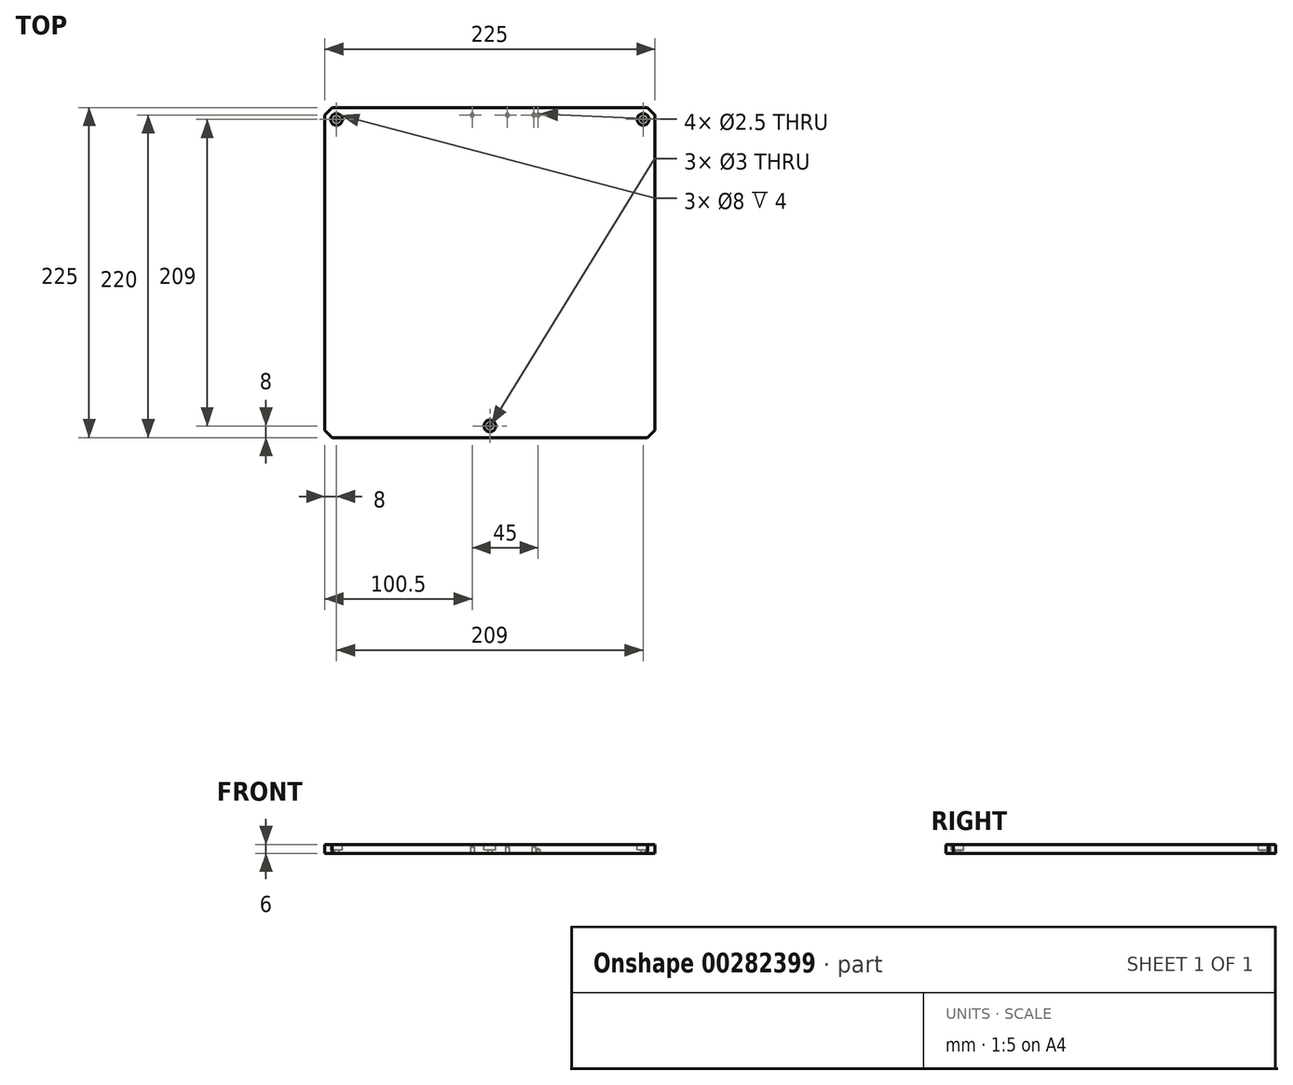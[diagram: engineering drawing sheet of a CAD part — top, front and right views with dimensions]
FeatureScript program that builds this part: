
annotation { "Feature Type Name" : "Feature", "Feature Type Description" : "" }
export const myFeature = defineFeature(function(context is Context, id is Id, definition is map)
    precondition{}
    {
        {
            var Q0;
            Q0=qCreatedBy(makeId("Top.planeOp"),FACE);
            var sketch = newSketch(context, id + "F0", { "sketchPlane" : qUnion([Q0])});
            skLineSegment(sketch, "E0.bottom", {"start": v(0, 0) * mm, "end": v(225, 0) * mm});
            skLineSegment(sketch, "E0.top", {"start": v(0, 225) * mm, "end": v(225, 225) * mm});
            skLineSegment(sketch, "E0.left", {"start": v(0, 0) * mm, "end": v(0, 225) * mm});
            skLineSegment(sketch, "E0.right", {"start": v(225, 0) * mm, "end": v(225, 225) * mm});
            skLineSegment(sketch, "E1", {"start": v(0, 225) * mm, "end": v(225, 0) * mm, "construction": true});
            skLineSegment(sketch, "E2", {"start": v(0, 0) * mm, "end": v(225, 225) * mm, "construction": true});
            skLineSegment(sketch, "E3", {"start": v(112.5, 225) * mm, "end": v(112.5, 0) * mm, "construction": true});
            skCircle(sketch, "E4", {"center": v(8, 217) * mm, "radius": 1.5 * mm});
            skCircle(sketch, "E5", {"center": v(217, 217) * mm, "radius": 1.5 * mm});
            skCircle(sketch, "E6", {"center": v(112.5, 8) * mm, "radius": 1.5 * mm});
            skSolve(sketch);
        }
        {
            var Q0;
            Q0=qSketchRegion(id+"F0",true);
            extrude(context, id + "F1", {"entities" : qUnion([Q0]), "depth" : 6 * mm});
        }
        {
            var Q0;
            Q0=makeQuery(id+"F1.opExtrude","CAP_FACE",FACE,{"disambiguationData":[OSD([sQuery(id+"F0.wireOp",EDGE,"E0.bottom"),sQuery(id+"F0.wireOp",EDGE,"E0.top"),sQuery(id+"F0.wireOp",EDGE,"E0.left"),sQuery(id+"F0.wireOp",EDGE,"E0.right"),sQuery(id+"F0.wireOp",EDGE,"E4"),sQuery(id+"F0.wireOp",EDGE,"E5"),sQuery(id+"F0.wireOp",EDGE,"Zo3WfQfq-pkXe-2Bfn-fg5S-mHa09XyBqBsQ"),sQuery(id+"F0.wireOp",EDGE,"XlddhZ3R-kbGH-BxdO-0Tjn-xPMr2SYzn92N"),sQuery(id+"F0.wireOp",EDGE,"E6")])],"isStart":false});
            var sketch = newSketch(context, id + "F2", { "sketchPlane" : qUnion([Q0])});
            skCircle(sketch, "E7", {"center": v(112.5, 8) * mm, "radius": 4 * mm});
            skCircle(sketch, "E8", {"center": v(8, 217) * mm, "radius": 4 * mm});
            skCircle(sketch, "E9", {"center": v(217, 217) * mm, "radius": 4 * mm});
            skSolve(sketch);
        }
        {
            var Q0;
            Q0=qSketchRegion(id+"F2",true);
            extrude(context, id + "F3", {"entities" : qUnion([Q0]), "operationType" : NewBodyOperationType.REMOVE, "oppositeDirection" : true, "depth" : 4 * mm});
        }
        {
            var Q0;
            Q0=makeQuery(id+"F1.opExtrude","SWEPT_EDGE",EDGE,{"disambiguationData":[OSD([sQuery(id+"F0.wireOp",EDGE,"E0.bottom"),sQuery(id+"F0.wireOp",EDGE,"E0.right")])]});
            var Q1;
            Q1=makeQuery(id+"F1.opExtrude","SWEPT_EDGE",EDGE,{"disambiguationData":[OSD([sQuery(id+"F0.wireOp",EDGE,"E0.bottom"),sQuery(id+"F0.wireOp",EDGE,"E0.left")])]});
            var Q2;
            Q2=makeQuery(id+"F1.opExtrude","SWEPT_EDGE",EDGE,{"disambiguationData":[OSD([sQuery(id+"F0.wireOp",EDGE,"E0.top"),sQuery(id+"F0.wireOp",EDGE,"E0.right")])]});
            var Q3;
            Q3=makeQuery(id+"F1.opExtrude","SWEPT_EDGE",EDGE,{"disambiguationData":[OSD([sQuery(id+"F0.wireOp",EDGE,"E0.top"),sQuery(id+"F0.wireOp",EDGE,"E0.left")])]});
            chamfer(context, id + "F4", {"entities" : qUnion([Q0, Q1, Q2, Q3]), "width" : 5 * mm, "tangentPropagation" : true});
        }
        {
            var Q0;
            Q0=makeQuery(id+"F1.opExtrude","CAP_FACE",FACE,{"disambiguationData":[OSD([sQuery(id+"F0.wireOp",EDGE,"E0.bottom"),sQuery(id+"F0.wireOp",EDGE,"E0.top"),sQuery(id+"F0.wireOp",EDGE,"E0.left"),sQuery(id+"F0.wireOp",EDGE,"E0.right"),sQuery(id+"F0.wireOp",EDGE,"E4"),sQuery(id+"F0.wireOp",EDGE,"E5"),sQuery(id+"F0.wireOp",EDGE,"E6")])],"isStart":true});
            var sketch = newSketch(context, id + "F5", { "sketchPlane" : qUnion([Q0])});
            skLineSegment(sketch, "E10", {"start": v(0, -220) * mm, "end": v(225, -220) * mm, "construction": true});
            skLineSegment(sketch, "E11", {"start": v(112.5, 0) * mm, "end": v(112.5, -225) * mm, "construction": true});
            skPoint(sketch, "E12", {"position": v(100.5, -220) * mm});
            skPoint(sketch, "E13", {"position": v(124.5, -220) * mm});
            skPoint(sketch, "E14", {"position": v(142.5, -220) * mm});
            skPoint(sketch, "E15", {"position": v(145.5, -220) * mm});
            skSolve(sketch);
        }
        {
            var Q0;
            Q0=sQuery(id+"F5.wireOp",VERTEX,"E12");
            var Q1;
            Q1=sQuery(id+"F5.wireOp",VERTEX,"E13");
            var Q2;
            Q2=sQuery(id+"F5.wireOp",VERTEX,"E14");
            var Q3;
            Q3=makeQuery(id+"F1.opExtrude","SWEPT_BODY",BODY,{"disambiguationData":[OSD([sQuery(id+"F0.wireOp",EDGE,"E0.bottom"),sQuery(id+"F0.wireOp",EDGE,"E0.top"),sQuery(id+"F0.wireOp",EDGE,"E0.left"),sQuery(id+"F0.wireOp",EDGE,"E0.right"),sQuery(id+"F0.wireOp",EDGE,"E4"),sQuery(id+"F0.wireOp",EDGE,"E5"),sQuery(id+"F0.wireOp",EDGE,"E6")])]});
            hole(context, id + "F6", {"style" : HoleStyle.SIMPLE, "endStyle" : HoleEndStyle.BLIND, "standardTappedOrClearance" : lookupTablePath({ "standard" : "ISO", "engagement" : "75%", "pitch" : "0.5 mm", "size" : "M3", "type" : "Tapped" }), "standardBlindInLast" : lookupTablePath({ "standard" : "ISO", "engagement" : "75%", "pitch" : "0.5 mm", "size" : "M3", "type" : "Tapped" }), "holeDiameter" : 2.5 * mm, "showTappedDepth" : true, "holeDepth" : 4.5 * mm, "tappedDepth" : 3 * mm, "tapClearance" : 3, "startFromSketch" : true, "locations" : qUnion([Q0, Q1, Q2]), "scope" : qUnion([Q3]), "majorDiameter" : 3 * mm});
        }
        {
            var Q0;
            Q0=sQuery(id+"F5.wireOp",VERTEX,"E15");
            var Q1;
            Q1=makeQuery(id+"F1.opExtrude","SWEPT_BODY",BODY,{"disambiguationData":[OSD([sQuery(id+"F0.wireOp",EDGE,"E0.bottom"),sQuery(id+"F0.wireOp",EDGE,"E0.top"),sQuery(id+"F0.wireOp",EDGE,"E0.left"),sQuery(id+"F0.wireOp",EDGE,"E0.right"),sQuery(id+"F0.wireOp",EDGE,"E4"),sQuery(id+"F0.wireOp",EDGE,"E5"),sQuery(id+"F0.wireOp",EDGE,"E6")])]});
            hole(context, id + "F7", {"style" : HoleStyle.SIMPLE, "endStyle" : HoleEndStyle.BLIND, "holeDiameter" : 2.5 * mm, "holeDepth" : 2.5 * mm, "tappedDepth" : 0.7 * mm, "tapClearance" : 3, "startFromSketch" : true, "locations" : qUnion([Q0]), "scope" : qUnion([Q1])});
        }
    });
